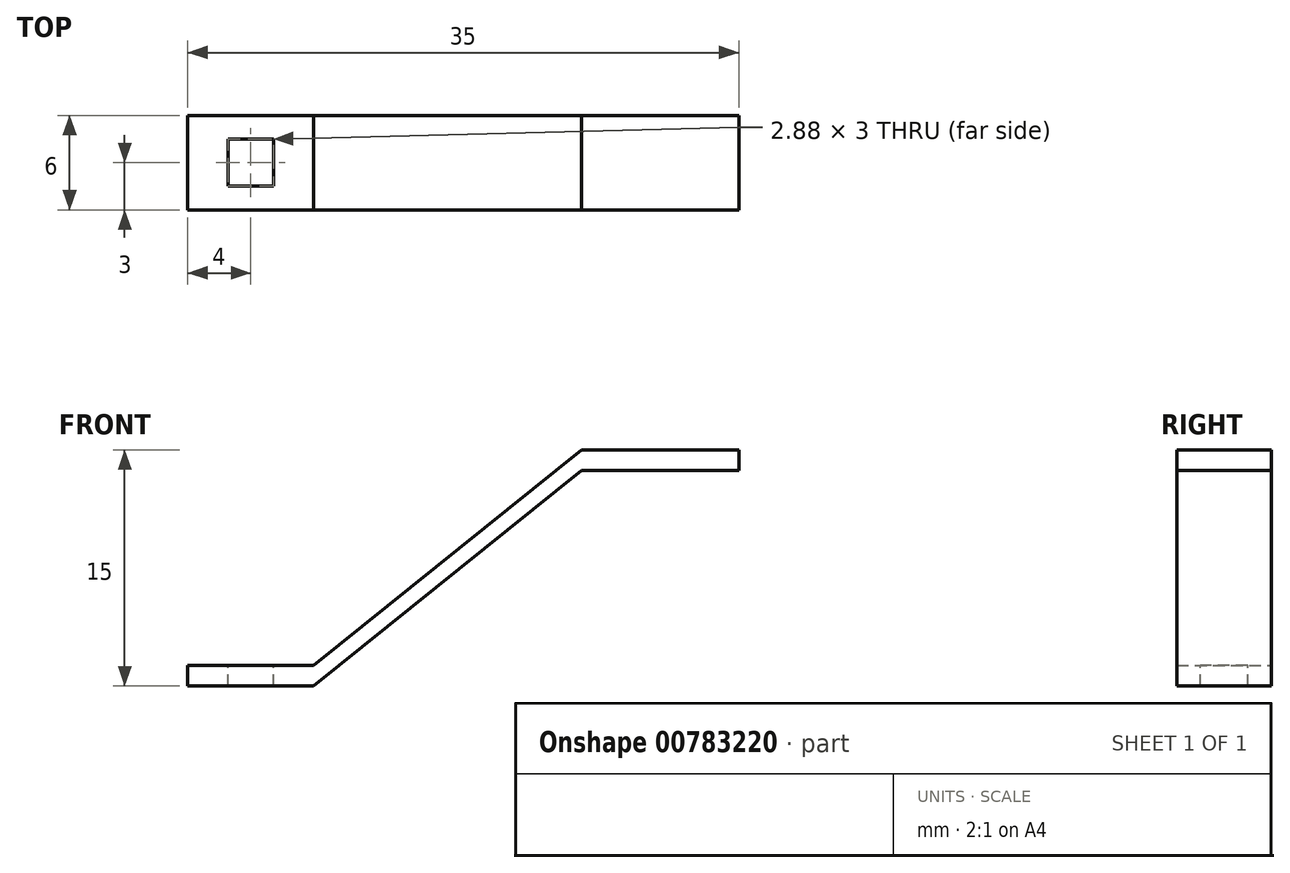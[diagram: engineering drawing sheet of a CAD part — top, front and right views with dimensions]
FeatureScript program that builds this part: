
annotation { "Feature Type Name" : "Feature", "Feature Type Description" : "" }
export const myFeature = defineFeature(function(context is Context, id is Id, definition is map)
    precondition{}
    {
        {
            var Q0;
            Q0=qCreatedBy(makeId("Front.planeOp"),FACE);
            var sketch = newSketch(context, id + "F0", { "sketchPlane" : qUnion([Q0])});
            skLineSegment(sketch, "E0", {"start": v(-4, 0) * mm, "end": v(-4, 1.3) * mm});
            skLineSegment(sketch, "E1", {"start": v(4, 1.3) * mm, "end": v(21, 15) * mm});
            skLineSegment(sketch, "E2", {"start": v(21, 15) * mm, "end": v(31, 15) * mm});
            skLineSegment(sketch, "E3", {"start": v(31, 15) * mm, "end": v(31, 13.7) * mm});
            skLineSegment(sketch, "E4", {"start": v(31, 13.7) * mm, "end": v(21, 13.7) * mm});
            skLineSegment(sketch, "E5", {"start": v(21, 13.7) * mm, "end": v(4, 0) * mm});
            skLineSegment(sketch, "E6", {"start": v(4, 0) * mm, "end": v(-4, 0) * mm});
            skLineSegment(sketch, "E7", {"start": v(-4, 1.3) * mm, "end": v(0, 1.3) * mm});
            skLineSegment(sketch, "E8", {"start": v(0, 1.3) * mm, "end": v(4, 1.3) * mm});
            skSolve(sketch);
        }
        {
            var Q0;
            Q0 = qSketchRegion(id + "F0", true);
            extrude(context, id + "F1", {"entities" : qUnion([Q0]), "depth" : 6 * mm, "offsetDistance" : 25 * mm});
        }
        {
            var Q0;
            Q0=makeQuery(id+"F1.opExtrude","SWEPT_FACE",FACE,{"disambiguationData":[OSD([sQuery(id+"F0.wireOp",EDGE,"E7"),sQuery(id+"F0.wireOp",EDGE,"E8")])]});
            var sketch = newSketch(context, id + "F2", { "sketchPlane" : qUnion([Q0])});
            skLineSegment(sketch, "E9.bottom", {"start": v(-1.44, -1.5) * mm, "end": v(1.44, -1.5) * mm});
            skLineSegment(sketch, "E9.top", {"start": v(-1.44, -4.5) * mm, "end": v(1.44, -4.5) * mm});
            skLineSegment(sketch, "E9.left", {"start": v(-1.44, -1.5) * mm, "end": v(-1.44, -4.5) * mm});
            skLineSegment(sketch, "E9.right", {"start": v(1.44, -1.5) * mm, "end": v(1.44, -4.5) * mm});
            skPoint(sketch, "E9.middle", {"position": v(0, -3) * mm});
            skSolve(sketch);
        }
        {
            var Q0;
            Q0=makeQuery(id+"F2.imprint","IMPRINT",FACE,{"disambiguationData":[TD([[makeQuery(id+"F2.imprint","IMPRINT",EDGE,{"derivedFrom":sQuery(id+"F2.wireOp",EDGE,"E9.bottom")}),-1.0]])]});
            extrude(context, id + "F3", {"entities" : qUnion([Q0]), "operationType" : NewBodyOperationType.REMOVE, "oppositeDirection" : true, "depth" : 1.3 * mm, "offsetDistance" : 25 * mm});
        }
    });
